annotation { "Feature Type Name" : "Feature", "Feature Type Description" : "" }
export const myFeature = defineFeature(function(context is Context, id is Id, definition is map)
    precondition{}
    {
        {
            var Q0;
            Q0=qCreatedBy(makeId("Front.planeOp"),FACE);
            var sketch = newSketch(context, id + "F0", { "sketchPlane" : qUnion([Q0])});
            skLineSegment(sketch, "E0", {"start": v(0, 0) * mm, "end": v(8.4, 114) * mm});
            skLineSegment(sketch, "E1", {"start": v(0, 0) * mm, "end": v(44.33, -3.27) * mm});
            skCircle(sketch, "E2", {"center": v(8.4, 114) * mm, "radius": 9.53 * mm});
            skCircle(sketch, "E3", {"center": v(4.67, 63.33) * mm, "radius": 15.88 * mm});
            skCircle(sketch, "E4", {"center": v(0, 0) * mm, "radius": 11.2 * mm});
            skCircle(sketch, "E5", {"center": v(44.33, -3.27) * mm, "radius": 7.94 * mm});
            skLineSegment(sketch, "E6", {"start": v(17.92, 114.48) * mm, "end": v(20.52, 64.15) * mm});
            skLineSegment(sketch, "E7", {"start": v(-0.93, 115.87) * mm, "end": v(-10.9, 66.47) * mm});
            skLineSegment(sketch, "E8", {"start": v(-11.2, 63.33) * mm, "end": v(-11.2, 0) * mm});
            skLineSegment(sketch, "E9", {"start": v(13.9, 17.3) * mm, "end": v(20.37, 61) * mm});
            skLineSegment(sketch, "E10", {"start": v(20.6, 8.28) * mm, "end": v(45.5, 4.58) * mm});
            skLineSegment(sketch, "E11", {"start": v(0, -11.2) * mm, "end": v(44.33, -11.2) * mm});
            skCircle(sketch, "E12", {"center": v(8.4, 114) * mm, "radius": 3.18 * mm});
            skCircle(sketch, "E13", {"center": v(4.67, 63.33) * mm, "radius": 3.18 * mm});
            skCircle(sketch, "E14", {"center": v(0, 0) * mm, "radius": 3.18 * mm});
            skCircle(sketch, "E15", {"center": v(44.33, -3.27) * mm, "radius": 3.18 * mm});
            skArc(sketch, "E16.filletArc", {"start": v(13.9, 17.3) * mm, "mid": v(15.37, 11.4) * mm, "end": v(20.6, 8.28) * mm});
            skCircle(sketch, "E17", {"center": v(4.18, 99.85) * mm, "radius": 3.18 * mm});
            skText(sketch, "E18", { "text": "Jill Dougherty", "fontName": "OpenSans-Regular.ttf"});
            skText(sketch, "E19", { "text": "volume= .734 in^3", "fontName": "OpenSans-Regular.ttf"});
            const initialGuessF0  = {"E18": [-0.09735, 0.16197, 1, 0, 0.00779], "E19": [-0.00474, 0.15802, 1, 0, 0.01271]};
            skSetInitialGuess(sketch, initialGuessF0);
            skSolve(sketch);
        }
        {
            var Q0;
            Q0 = qSketchRegion(id + "F0", true);
            var Q1;
            {var subQ0=sQuery(id+"F0.wireOp",EDGE,"E14");var subQ1=sQuery(id+"F0.wireOp",EDGE,"E0");var subQ2=makeQuery(id+"F0.imprint","INTERSECT",VERTEX,{"derivedFrom":[subQ1,subQ0]});Q1=makeQuery(id+"F0.imprint","IMPRINT",FACE,{"disambiguationData":[TD([[makeQuery(id+"F0.imprint","IMPRINT",EDGE,{"disambiguationData":[TD([[subQ2,-1.0]])],"derivedFrom":subQ1}),-1.0]])]});}
            extrude(context, id + "F1", {"entities" : qUnion([Q0, Q1]), "depth" : 3.05 * mm, "offsetDistance" : 25.4 * mm});
        }
    });